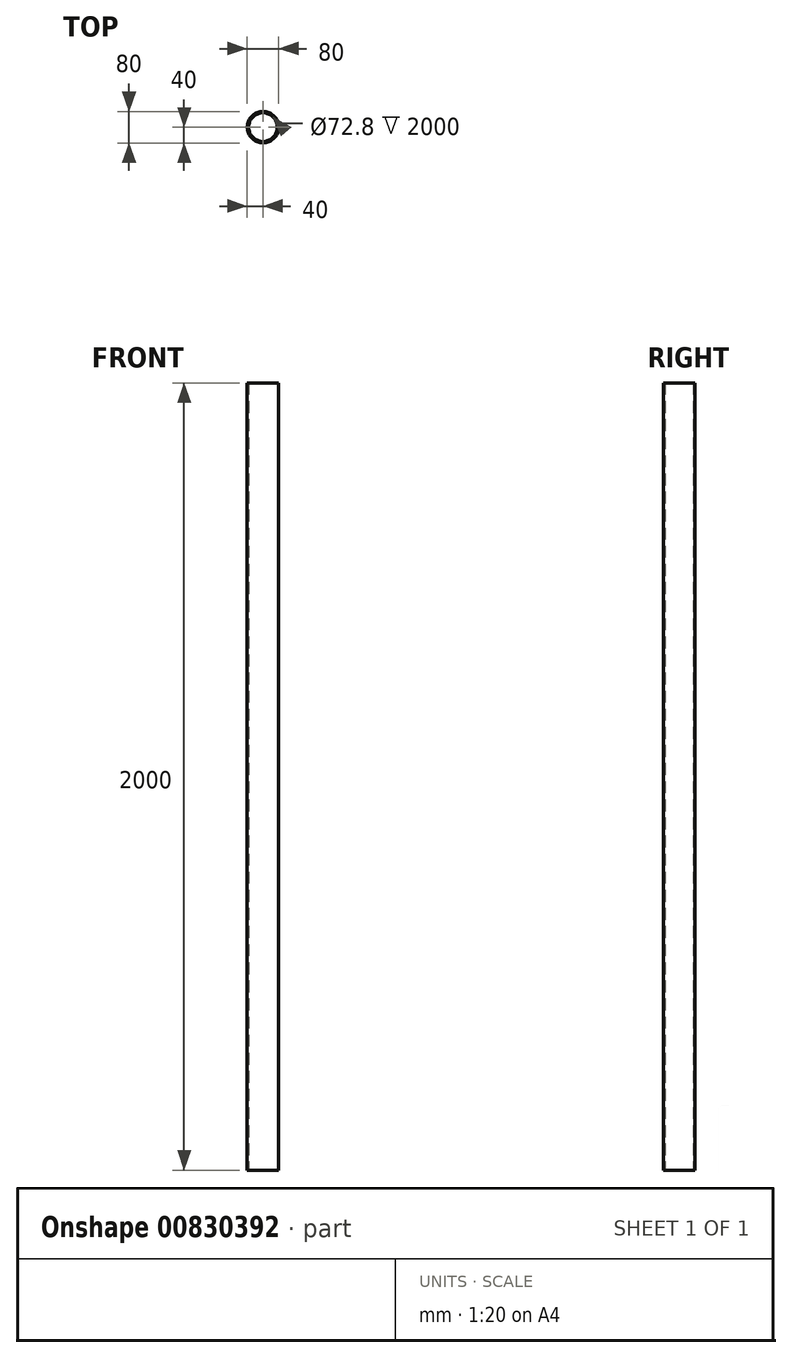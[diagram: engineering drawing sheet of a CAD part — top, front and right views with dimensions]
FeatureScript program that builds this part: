
annotation { "Feature Type Name" : "Feature", "Feature Type Description" : "" }
export const myFeature = defineFeature(function(context is Context, id is Id, definition is map)
    precondition{}
    {
        {
            var Q0;
            Q0=qCreatedBy(makeId("Top.planeOp"),FACE);
            var sketch = newSketch(context, id + "F0", { "sketchPlane" : qUnion([Q0])});
            skCircle(sketch, "E0", {"center": v(0, 0) * mm, "radius": 40 * mm});
            skCircle(sketch, "E1.0", {"center": v(0, 0) * mm, "radius": 36.4 * mm});
            skSolve(sketch);
        }
        {
            var Q0;
            Q0 = qSketchRegion(id + "F0", true);
            extrude(context, id + "F1", {"entities" : qUnion([Q0]), "depth" : 2000 * mm, "offsetDistance" : 25 * mm});
        }
    });
